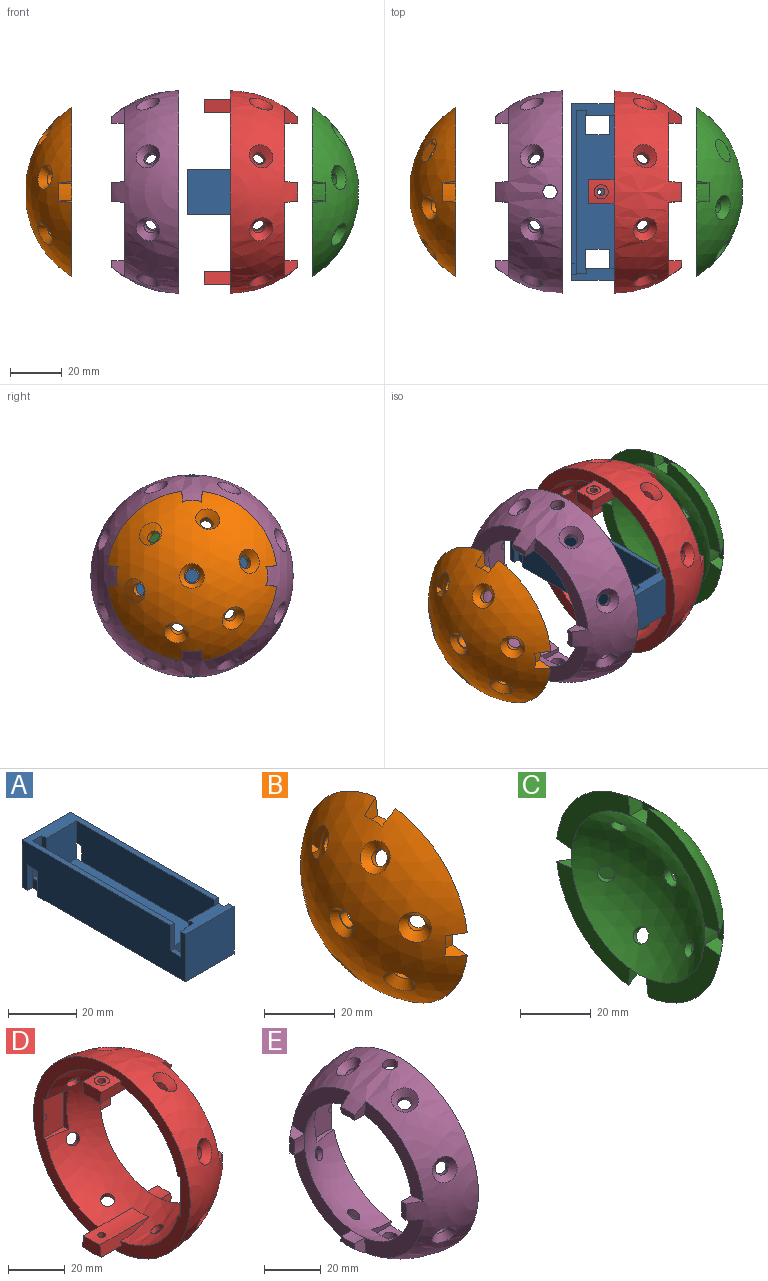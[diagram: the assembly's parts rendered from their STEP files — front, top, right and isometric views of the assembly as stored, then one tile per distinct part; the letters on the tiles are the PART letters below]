
ASSEMBLY  parts=5 mates=4
PART A: 43 faces, bbox 20x67.9x17 mm
  f0: plane 61.42x20mm, normal (0,0,1), area 280.7mm2, adj f1,f4,f6,f7,f10,f11,f14,f15
  f1: plane 67.93x17mm, normal (-1,0,0), area 1075.1mm2, adj f0,f3,f8,f9,f10,f35,f36,f37
  f2: plane 63x16.5mm, normal (0,0,1), area 848.9mm2, adj f5,f6,f7,f11,f12,f13,f14,f15
  f3: plane 67.93x20mm, normal (0,0,-1), area 1193.3mm2, adj f1,f4,f9,f10,f17,f18,f19,f20
  f4: plane 67.93x17mm, normal (1,0,0), area 1075.1mm2, adj f0,f3,f8,f9,f10,f27,f28,f29
  f5: plane 13.5x12.56mm, normal (0,1,0), area 167.2mm2, adj f2,f6,f8,f13,f16,f32,f34
  f6: plane 59x13.5mm, normal (-1,0,0), area 765.7mm2, adj f0,f2,f5,f7,f28,f29,f33,f34
  f7: plane 13.5x12.56mm, normal (0,-1,0), area 168.1mm2, adj f0,f2,f6,f14,f21,f29,f30
  f8: plane 20x4.46mm, normal (0,0,1), area 72.6mm2, adj f1,f4,f5,f9,f12,f13,f31,f32
  f9: plane 20x17mm, normal (0,-1,0), area 340mm2, adj f1,f3,f4,f8
  f10: plane 20x17mm, normal (0,1,0), area 340mm2, adj f0,f1,f3,f4
  f11: plane 63x13.5mm, normal (1,0,0), area 790mm2, adj f0,f2,f12,f15,f36,f37,f40,f41
  f12: plane 13.5x3.94mm, normal (0,1,0), area 50.9mm2, adj f2,f8,f11,f13,f41,f42
  f13: plane 13.5x2mm, normal (-1,0,0), area 27mm2, adj f2,f5,f8,f12,f16
  f14: plane 13.5x2mm, normal (-1,0,0), area 27mm2, adj f0,f2,f7,f15,f21
  f15: plane 13.5x3.94mm, normal (0,-1,0), area 51.8mm2, adj f0,f2,f11,f14,f37,f38
  f16: plane 8.81x0.51mm, normal (0,0,-1), area 4.5mm2, adj f5,f13,f18,f19
  f17: plane 9x3.5mm, normal (0,-1,0), area 31.5mm2, adj f2,f3,f18,f20
  f18: plane 7.87x3.5mm, normal (-1,0,0), area 27.6mm2, adj f2,f3,f16,f17,f19
  f19: plane 9x3.5mm, normal (0,1,0), area 31.5mm2, adj f2,f3,f16,f18,f20
  f20: plane 7.87x3.5mm, normal (1,0,0), area 27.6mm2, adj f2,f3,f17,f19
  f21: plane 8.81x0.51mm, normal (0,0,-1), area 4.5mm2, adj f7,f14,f22,f25
  f22: plane 7.87x3.5mm, normal (-1,0,0), area 27.6mm2, adj f2,f3,f21,f23,f25
  f23: plane 9x3.5mm, normal (0,1,0), area 31.5mm2, adj f2,f3,f22,f24
  f24: plane 7.87x3.5mm, normal (1,0,0), area 27.6mm2, adj f2,f3,f23,f25
  f25: plane 9x3.5mm, normal (0,-1,0), area 31.5mm2, adj f2,f3,f21,f22,f24
  f26: cylinder r=1.4mm len=3.5mm, axis (0,0,1), area 30.7mm2, adj f2,f3
  f27: plane 9.15x2mm, normal (0,-1,0), area 18.3mm2, adj f3,f4,f29,f30
  f28: plane 9.15x2mm, normal (0,1,0), area 16.9mm2, adj f2,f3,f4,f6,f29,f30
  f29: plane 4.35x2mm, normal (0,0,-1), area 8.2mm2, adj f4,f6,f7,f27,f28,f30
  f30: plane 9.15x4.35mm, normal (1,0,0), area 27.6mm2, adj f2,f3,f7,f27,f28,f29
  f31: plane 9.15x2mm, normal (0,1,0), area 18.3mm2, adj f4,f8,f32,f34
  f32: plane 9.15x2.31mm, normal (1,0,0), area 21.2mm2, adj f5,f8,f31,f34
  f33: plane 9.15x1.75mm, normal (0,-1,0), area 16mm2, adj f0,f4,f6,f34
  f34: plane 4.35x2mm, normal (0,0,1), area 8.2mm2, adj f4,f5,f6,f31,f32,f33
  f35: plane 9.15x2mm, normal (0,-1,0), area 18.3mm2, adj f1,f3,f37,f38
  f36: plane 9.15x2mm, normal (0,1,0), area 16.9mm2, adj f1,f2,f3,f11,f37,f38
  f37: plane 4.35x2mm, normal (0,0,-1), area 7.7mm2, adj f1,f11,f15,f35,f36,f38
  f38: plane 9.15x4.35mm, normal (-1,0,0), area 16.3mm2, adj f2,f3,f15,f35,f36,f37
  f39: plane 9.15x2mm, normal (0,1,0), area 18.3mm2, adj f1,f8,f41,f42
  f40: plane 9.15x1.75mm, normal (0,-1,0), area 16mm2, adj f0,f1,f11,f41
  f41: plane 4.35x2mm, normal (0,0,1), area 7.7mm2, adj f1,f11,f12,f39,f40,f42
  f42: plane 9.15x0.31mm, normal (-1,0,0), area 2.9mm2, adj f8,f12,f39,f41
PART B: 38 faces, bbox 28.1x65.9x66.2 mm
  f0: sphere r=39mm, area 3715.4mm2, adj f1,f2,f3,f4,f6,f10,f12,f14
  f1: plane 29.36x29.36mm, normal (1,0,0), area 242.1mm2, adj f0,f5,f24,f28
  f2: plane 29.36x29.36mm, normal (1,0,0), area 242.1mm2, adj f0,f5,f23,f34
  f3: plane 29.36x29.36mm, normal (1,0,0), area 242.1mm2, adj f0,f5,f27,f32
  f4: plane 29.36x29.36mm, normal (1,0,0), area 242.1mm2, adj f0,f5,f31,f35
  f5: sphere r=34mm, area 2634mm2, adj f1,f2,f3,f4,f9,f11,f13,f15
  f6: cone r=2.5mm half-angle=39.8deg, axis (-1,0,0), area 69.3mm2, adj f0,f7
  f7: plane 5.83x5.83mm, normal (-1,0,0), area 7.1mm2, adj f6,f8
  f8: cylinder r=2.5mm len=5mm, axis (-1,0,0), area 40.7mm2, adj f7,f9
  f9: plane 5.21x5.21mm, normal (1,0,0), area 1.7mm2, adj f5,f8
  f10: cone r=2.5mm half-angle=39.8deg, axis (-0.81,-0.41,-0.42), area 80.4mm2, adj f0,f11
  f11: cylinder r=2.5mm len=5.42mm, axis (-0.81,-0.41,-0.42), area 32.9mm2, adj f5,f10
  f12: cone r=2.5mm half-angle=39.8deg, axis (-0.81,0.41,0.42), area 80.4mm2, adj f0,f13
  f13: cylinder r=2.5mm len=5.42mm, axis (-0.81,0.41,0.42), area 32.9mm2, adj f5,f12
  f14: cone r=2.5mm half-angle=39.8deg, axis (-0.81,0.16,-0.57), area 80.4mm2, adj f0,f15
  f15: cylinder r=2.5mm len=5.31mm, axis (-0.81,0.16,-0.57), area 32.9mm2, adj f5,f14
  f16: cone r=2.5mm half-angle=39.8deg, axis (-0.81,-0.16,0.57), area 80.4mm2, adj f0,f17
  f17: cylinder r=2.5mm len=5.31mm, axis (-0.81,-0.16,0.57), area 32.9mm2, adj f5,f16
  f18: cone r=2.5mm half-angle=39.8deg, axis (-0.81,0.57,-0.15), area 80.4mm2, adj f0,f19
  f19: cylinder r=2.5mm len=5.3mm, axis (-0.81,0.57,-0.15), area 32.9mm2, adj f5,f18
  f20: cone r=2.5mm half-angle=39.8deg, axis (-0.81,-0.57,0.15), area 80.4mm2, adj f0,f21
  f21: cylinder r=2.5mm len=5.3mm, axis (-0.81,-0.57,0.15), area 32.9mm2, adj f5,f20
  f22: plane 7.73x3.18mm, normal (1,0,0), area 15.9mm2, adj f0,f23,f24,f25
  f23: plane 6.21x5.13mm, normal (0,-0.12,0.99), area 21.7mm2, adj f0,f2,f22,f25
  f24: plane 6.21x5.13mm, normal (0,-0.12,-0.99), area 21.7mm2, adj f0,f1,f22,f25
  f25: cylinder r=26.74mm len=6.52mm, axis (1,0,0), area 32.7mm2, adj f5,f22,f23,f24
  f26: plane 7.38x2.82mm, normal (1,0,0), area 15.9mm2, adj f0,f27,f28,f29
  f27: plane 6.1x5.02mm, normal (0,-0.99,0.12), area 21.7mm2, adj f0,f3,f26,f29
  f28: plane 6.1x5.02mm, normal (0,0.99,0.12), area 21.7mm2, adj f0,f1,f26,f29
  f29: cylinder r=26.74mm len=6.52mm, axis (1,0,0), area 32.7mm2, adj f5,f26,f27,f28
  f30: plane 7.73x3.18mm, normal (1,0,0), area 15.9mm2, adj f0,f31,f32,f33
  f31: plane 6.21x5.13mm, normal (0,0.12,0.99), area 21.7mm2, adj f0,f4,f30,f33
  f32: plane 6.21x5.13mm, normal (0,0.12,-0.99), area 21.7mm2, adj f0,f3,f30,f33
  f33: cylinder r=26.74mm len=6.52mm, axis (1,0,0), area 32.7mm2, adj f5,f30,f31,f32
  f34: plane 6.1x5.02mm, normal (0,0.99,-0.12), area 21.7mm2, adj f0,f2,f36,f37
  f35: plane 6.1x5.02mm, normal (0,-0.99,-0.12), area 21.7mm2, adj f0,f4,f36,f37
  f36: plane 7.38x2.82mm, normal (1,0,0), area 15.9mm2, adj f0,f34,f35,f37
  f37: cylinder r=26.74mm len=6.52mm, axis (1,0,0), area 32.7mm2, adj f5,f34,f35,f36
PART C: 38 faces, bbox 28.1x65.9x66.2 mm
  f0: plane 29.36x29.36mm, normal (-1,0,0), area 242.1mm2, adj f4,f5,f24,f35
  f1: plane 29.36x29.36mm, normal (-1,0,0), area 242.1mm2, adj f4,f5,f23,f28
  f2: plane 29.36x29.36mm, normal (-1,0,0), area 242.1mm2, adj f4,f5,f27,f32
  f3: plane 29.36x29.36mm, normal (-1,0,0), area 242.1mm2, adj f4,f5,f31,f34
  f4: sphere r=34mm, area 2712.6mm2, adj f0,f1,f2,f3,f9,f11,f13,f15
  f5: sphere r=39mm, area 3715.3mm2, adj f0,f1,f2,f3,f6,f10,f12,f14
  f6: cone r=2.5mm half-angle=39.8deg, axis (1,0,0), area 69.3mm2, adj f5,f7
  f7: plane 5.83x5.83mm, normal (1,0,0), area 7.1mm2, adj f6,f8
  f8: cylinder r=2.5mm len=5mm, axis (1,0,0), area 40.7mm2, adj f7,f9
  f9: plane 5.21x5.21mm, normal (-1,0,0), area 1.7mm2, adj f4,f8
  f10: cone r=2.5mm half-angle=39.8deg, axis (0.81,-0.41,-0.42), area 80.4mm2, adj f5,f11
  f11: cylinder r=2.5mm len=5.42mm, axis (0.81,-0.41,-0.42), area 32.9mm2, adj f4,f10
  f12: cone r=2.5mm half-angle=39.8deg, axis (0.81,0.41,0.42), area 80.4mm2, adj f5,f13
  f13: cylinder r=2.5mm len=5.42mm, axis (0.81,0.41,0.42), area 32.9mm2, adj f4,f12
  f14: cone r=2.5mm half-angle=39.8deg, axis (0.81,0.16,-0.57), area 80.4mm2, adj f5,f15
  f15: cylinder r=2.5mm len=5.31mm, axis (0.81,0.16,-0.57), area 32.9mm2, adj f4,f14
  f16: cone r=2.5mm half-angle=39.8deg, axis (0.81,-0.16,0.57), area 80.4mm2, adj f5,f17
  f17: cylinder r=2.5mm len=5.31mm, axis (0.81,-0.16,0.57), area 32.9mm2, adj f4,f16
  f18: cone r=2.5mm half-angle=39.8deg, axis (0.81,0.57,-0.15), area 80.4mm2, adj f5,f19
  f19: cylinder r=2.5mm len=5.3mm, axis (0.81,0.57,-0.15), area 32.9mm2, adj f4,f18
  f20: cone r=2.5mm half-angle=39.8deg, axis (0.81,-0.57,0.15), area 80.4mm2, adj f5,f21
  f21: cylinder r=2.5mm len=5.3mm, axis (0.81,-0.57,0.15), area 32.9mm2, adj f4,f20
  f22: plane 7.73x3.18mm, normal (-1,0,0), area 15.9mm2, adj f5,f23,f24,f25
  f23: plane 6.21x5.13mm, normal (0,-0.12,-0.99), area 21.7mm2, adj f1,f5,f22,f25
  f24: plane 6.21x5.13mm, normal (0,-0.12,0.99), area 21.7mm2, adj f0,f5,f22,f25
  f25: cylinder r=26.74mm len=6.52mm, axis (-1,0,0), area 32.7mm2, adj f4,f22,f23,f24
  f26: plane 7.38x2.82mm, normal (-1,0,0), area 15.9mm2, adj f5,f27,f28,f29
  f27: plane 6.1x5.02mm, normal (0,-0.99,0.12), area 21.7mm2, adj f2,f5,f26,f29
  f28: plane 6.1x5.02mm, normal (0,0.99,0.12), area 21.7mm2, adj f1,f5,f26,f29
  f29: cylinder r=26.74mm len=6.52mm, axis (-1,0,0), area 32.7mm2, adj f4,f26,f27,f28
  f30: plane 7.73x3.18mm, normal (-1,0,0), area 15.9mm2, adj f5,f31,f32,f33
  f31: plane 6.21x5.13mm, normal (0,0.12,0.99), area 21.7mm2, adj f3,f5,f30,f33
  f32: plane 6.21x5.13mm, normal (0,0.12,-0.99), area 21.7mm2, adj f2,f5,f30,f33
  f33: cylinder r=26.74mm len=6.52mm, axis (-1,0,0), area 32.7mm2, adj f4,f30,f31,f32
  f34: plane 6.1x5.02mm, normal (0,-0.99,-0.12), area 21.7mm2, adj f3,f5,f36,f37
  f35: plane 6.1x5.02mm, normal (0,0.99,-0.12), area 21.7mm2, adj f0,f5,f36,f37
  f36: plane 7.38x2.82mm, normal (-1,0,0), area 15.9mm2, adj f5,f34,f35,f37
  f37: cylinder r=26.74mm len=6.52mm, axis (-1,0,0), area 32.7mm2, adj f4,f34,f35,f36
PART D: 69 faces, bbox 49x78x78 mm
  f0: cylinder r=30.8mm len=24.2mm, axis (-1,0,0), area 188.5mm2, adj f23,f34,f35,f36,f68
  f1: cylinder r=35.8mm len=10mm, axis (-1,0,0), area 70.1mm2, adj f6,f23,f34,f36,f65,f66,f67
  f2: cylinder r=35.8mm len=10mm, axis (-1,0,0), area 70.1mm2, adj f6,f25,f37,f39,f61,f62,f63
  f3: sphere r=34mm, area 4mm2, adj f6,f58
  f4: sphere r=34mm, area 4mm2, adj f6,f53
  f5: sphere r=34mm, area 3727.2mm2, adj f6,f19,f20,f21,f22,f26,f27,f28
  f6: plane 78x78mm, normal (-1,0,0), area 1102.7mm2, adj f1,f2,f3,f4,f5,f34,f36,f37
  f7: plane 6.1x5.02mm, normal (0,0.99,0.12), area 21.7mm2, adj f9,f22,f48,f49
  f8: plane 6.1x5.02mm, normal (0,-0.99,0.12), area 21.7mm2, adj f9,f19,f48,f49
  f9: plane 7.09x2.53mm, normal (1,0,0), area 15.9mm2, adj f7,f8,f48,f49
  f10: plane 6.08x5mm, normal (0,-0.12,-0.99), area 21.7mm2, adj f12,f22,f48,f50
  f11: plane 6.08x5mm, normal (0,-0.12,0.99), area 21.7mm2, adj f12,f21,f48,f50
  f12: plane 7.09x2.53mm, normal (1,0,0), area 15.9mm2, adj f10,f11,f48,f50
  f13: plane 6.1x5.02mm, normal (0,0.99,-0.12), area 21.7mm2, adj f15,f21,f48,f51
  f14: plane 6.1x5.02mm, normal (0,-0.99,-0.12), area 21.7mm2, adj f15,f20,f48,f51
  f15: plane 7.09x2.53mm, normal (1,0,0), area 15.9mm2, adj f13,f14,f48,f51
  f16: plane 6.08x5mm, normal (0,0.12,0.99), area 21.7mm2, adj f18,f20,f48,f52
  f17: plane 6.08x5mm, normal (0,0.12,-0.99), area 21.7mm2, adj f18,f19,f48,f52
  f18: plane 7.09x2.53mm, normal (1,0,0), area 15.9mm2, adj f16,f17,f48,f52
  f19: plane 29.36x29.36mm, normal (1,0,0), area 242.1mm2, adj f5,f8,f17,f48
  f20: plane 29.36x29.36mm, normal (1,0,0), area 242.1mm2, adj f5,f14,f16,f48
  f21: plane 29.36x29.36mm, normal (1,0,0), area 242.1mm2, adj f5,f11,f13,f48
  f22: plane 29.36x29.36mm, normal (1,0,0), area 242.1mm2, adj f5,f7,f10,f48
  f23: plane 9.35x5.26mm, normal (-1,0,0), area 43.6mm2, adj f0,f1,f34,f36
  f24: cylinder r=30.8mm len=24.2mm, axis (-1,0,0), area 188.5mm2, adj f25,f37,f38,f39,f64
  f25: plane 9.35x5.26mm, normal (-1,0,0), area 43.6mm2, adj f2,f24,f37,f39
  f26: cylinder r=2.5mm len=5.42mm, axis (0.31,0.37,-0.88), area 32.9mm2, adj f5,f40
  f27: cylinder r=2.5mm len=5.42mm, axis (0.31,-0.37,0.88), area 32.9mm2, adj f5,f41
  f28: cylinder r=2.5mm len=5.42mm, axis (0.31,-0.36,-0.88), area 32.9mm2, adj f5,f42
  f29: cylinder r=2.5mm len=5.42mm, axis (0.31,0.36,0.88), area 32.9mm2, adj f5,f43
  f30: cylinder r=2.5mm len=5.42mm, axis (0.31,-0.88,-0.37), area 32.9mm2, adj f5,f44
  f31: cylinder r=2.5mm len=5.42mm, axis (0.31,0.88,0.37), area 32.9mm2, adj f5,f45
  f32: cylinder r=2.5mm len=5.42mm, axis (0.31,-0.88,0.36), area 32.9mm2, adj f5,f46
  f33: cylinder r=2.5mm len=5.42mm, axis (0.31,0.88,-0.36), area 32.9mm2, adj f5,f47
  f34: plane 24.2x4.96mm, normal (0,-0.99,0.13), area 81mm2, adj f0,f1,f5,f6,f23,f35
  f35: plane 8.06x0.36mm, normal (1,0,0), area 0.7mm2, adj f0,f5,f34,f36
  f36: plane 24.2x4.96mm, normal (0,0.99,0.13), area 81mm2, adj f0,f1,f5,f6,f23,f35
  f37: plane 24.2x4.96mm, normal (0,0.99,-0.13), area 81mm2, adj f2,f5,f6,f24,f25,f38
  f38: plane 8.06x0.36mm, normal (1,0,0), area 0.7mm2, adj f5,f24,f37,f39
  f39: plane 24.2x4.96mm, normal (0,-0.99,-0.13), area 81mm2, adj f2,f5,f6,f24,f25,f38
  f40: cone r=2.5mm half-angle=39.8deg, axis (0.31,0.37,-0.88), area 80.4mm2, adj f26,f48
  f41: cone r=2.5mm half-angle=39.8deg, axis (0.31,-0.37,0.88), area 80.4mm2, adj f27,f48
  f42: cone r=2.5mm half-angle=39.8deg, axis (0.31,-0.36,-0.88), area 80.4mm2, adj f28,f48
  f43: cone r=2.5mm half-angle=39.8deg, axis (0.31,0.36,0.88), area 80.4mm2, adj f29,f48
  f44: cone r=2.5mm half-angle=39.8deg, axis (0.31,-0.88,-0.37), area 80.4mm2, adj f30,f48
  f45: cone r=2.5mm half-angle=39.8deg, axis (0.31,0.88,0.37), area 80.4mm2, adj f31,f48
  f46: cone r=2.5mm half-angle=39.8deg, axis (0.31,-0.88,0.36), area 80.4mm2, adj f32,f48
  f47: cone r=2.5mm half-angle=39.8deg, axis (0.31,0.88,-0.36), area 80.4mm2, adj f33,f48
  f48: sphere r=39mm, area 4765.4mm2, adj f6,f7,f8,f9,f10,f11,f12,f13
  f49: cylinder r=26.74mm len=6.52mm, axis (-1,0,0), area 32.7mm2, adj f5,f7,f8,f9
  f50: cylinder r=26.74mm len=6.52mm, axis (-1,0,0), area 32.7mm2, adj f5,f10,f11,f12
  f51: cylinder r=26.74mm len=6.52mm, axis (-1,0,0), area 32.7mm2, adj f5,f13,f14,f15
  f52: cylinder r=26.74mm len=6.52mm, axis (-1,0,0), area 32.7mm2, adj f5,f16,f17,f18
  f53: plane 17x10mm, normal (0,-1,0), area 166mm2, adj f4,f6,f54,f55,f56
  f54: plane 10x2.6mm, normal (0,0,-1), area 15.6mm2, adj f5,f6,f53,f56
  f55: plane 10x2.6mm, normal (0,0,1), area 15.6mm2, adj f5,f6,f53,f56
  f56: plane 17x2.6mm, normal (-1,0,0), area 31.3mm2, adj f5,f53,f54,f55
  f57: plane 10x2.6mm, normal (0,0,-1), area 15.6mm2, adj f5,f6,f58,f60
  f58: plane 17x10mm, normal (0,1,0), area 166mm2, adj f3,f6,f57,f59,f60
  f59: plane 10x2.6mm, normal (0,0,1), area 15.6mm2, adj f5,f6,f58,f60
  f60: plane 17x2.6mm, normal (-1,0,0), area 31.3mm2, adj f5,f57,f58,f59
  f61: cylinder r=2.75mm len=5.35mm, axis (0,0,1), area 0.4mm2, adj f2,f63
  f62: cylinder r=2.75mm len=5.35mm, axis (0,0,1), area 0.4mm2, adj f2,f63
  f63: plane 5.5x5.35mm, normal (0,0,1), area 17mm2, adj f2,f61,f62,f64
  f64: cylinder r=1.45mm len=4.93mm, axis (0,0,1), area 44.8mm2, adj f24,f63
  f65: cylinder r=2.75mm len=5.35mm, axis (0,0,-1), area 0.4mm2, adj f1,f67
  f66: cylinder r=2.75mm len=5.35mm, axis (0,0,-1), area 0.4mm2, adj f1,f67
  f67: plane 5.5x5.35mm, normal (0,0,-1), area 17mm2, adj f1,f65,f66,f68
  f68: cylinder r=1.45mm len=4.93mm, axis (0,0,-1), area 44.8mm2, adj f0,f67
PART E: 63 faces, bbox 39x78x78 mm
  f0: sphere r=39mm, area 4717.5mm2, adj f6,f7,f8,f9,f10,f11,f12,f13
  f1: cylinder r=35.8mm len=10mm, axis (-1,0,0), area 70.1mm2, adj f6,f46,f47,f48,f60,f61,f62
  f2: cylinder r=35.8mm len=10mm, axis (-1,0,0), area 70.1mm2, adj f6,f43,f44,f45,f57,f58,f59
  f3: sphere r=34mm, area 4mm2, adj f6,f54
  f4: sphere r=34mm, area 4mm2, adj f6,f49
  f5: sphere r=34mm, area 3802mm2, adj f6,f19,f20,f21,f22,f23,f24,f25
  f6: plane 78x78mm, normal (1,0,0), area 1102.7mm2, adj f0,f1,f2,f3,f4,f5,f43,f44
  f7: plane 6.1x5.02mm, normal (0,-0.99,0.12), area 21.7mm2, adj f0,f9,f20,f39
  f8: plane 6.1x5.02mm, normal (0,0.99,0.12), area 21.7mm2, adj f0,f9,f22,f39
  f9: plane 7.09x2.53mm, normal (-1,0,0), area 15.9mm2, adj f0,f7,f8,f39
  f10: plane 6.08x5mm, normal (0,-0.12,0.99), area 21.7mm2, adj f0,f12,f21,f40
  f11: plane 6.08x5mm, normal (0,-0.12,-0.99), area 21.7mm2, adj f0,f12,f22,f40
  f12: plane 7.09x2.53mm, normal (-1,0,0), area 15.9mm2, adj f0,f10,f11,f40
  f13: plane 6.1x5.02mm, normal (0,-0.99,-0.12), area 21.7mm2, adj f0,f15,f19,f41
  f14: plane 6.1x5.02mm, normal (0,0.99,-0.12), area 21.7mm2, adj f0,f15,f21,f41
  f15: plane 7.09x2.53mm, normal (-1,0,0), area 15.9mm2, adj f0,f13,f14,f41
  f16: plane 6.08x5mm, normal (0,0.12,-0.99), area 21.7mm2, adj f0,f18,f20,f42
  f17: plane 6.08x5mm, normal (0,0.12,0.99), area 21.7mm2, adj f0,f18,f19,f42
  f18: plane 7.09x2.53mm, normal (-1,0,0), area 15.9mm2, adj f0,f16,f17,f42
  f19: plane 29.36x29.36mm, normal (-1,0,0), area 242.1mm2, adj f0,f5,f13,f17
  f20: plane 29.36x29.36mm, normal (-1,0,0), area 242.1mm2, adj f0,f5,f7,f16
  f21: plane 29.36x29.36mm, normal (-1,0,0), area 242.1mm2, adj f0,f5,f10,f14
  f22: plane 29.36x29.36mm, normal (-1,0,0), area 242.1mm2, adj f0,f5,f8,f11
  f23: cylinder r=2.5mm len=5.42mm, axis (-0.31,-0.37,0.88), area 32.9mm2, adj f5,f32
  f24: cylinder r=2.5mm len=5.42mm, axis (-0.31,0.36,0.88), area 32.9mm2, adj f5,f34
  f25: cylinder r=2.5mm len=5.42mm, axis (-0.31,0.88,0.37), area 32.9mm2, adj f5,f36
  f26: cylinder r=2.5mm len=5.42mm, axis (-0.31,0.88,-0.36), area 32.9mm2, adj f5,f38
  f27: cylinder r=2.5mm len=5.42mm, axis (-0.31,-0.88,0.36), area 32.9mm2, adj f5,f37
  f28: cylinder r=2.5mm len=5.42mm, axis (-0.31,-0.88,-0.37), area 32.9mm2, adj f5,f35
  f29: cylinder r=2.5mm len=5.42mm, axis (-0.31,-0.36,-0.88), area 32.9mm2, adj f5,f33
  f30: cylinder r=2.5mm len=5.42mm, axis (-0.31,0.37,-0.88), area 32.9mm2, adj f5,f31
  f31: cone r=2.5mm half-angle=39.8deg, axis (-0.31,0.37,-0.88), area 80.4mm2, adj f0,f30
  f32: cone r=2.5mm half-angle=39.8deg, axis (-0.31,-0.37,0.88), area 80.4mm2, adj f0,f23
  f33: cone r=2.5mm half-angle=39.8deg, axis (-0.31,-0.36,-0.88), area 80.4mm2, adj f0,f29
  f34: cone r=2.5mm half-angle=39.8deg, axis (-0.31,0.36,0.88), area 80.4mm2, adj f0,f24
  f35: cone r=2.5mm half-angle=39.8deg, axis (-0.31,-0.88,-0.37), area 80.4mm2, adj f0,f28
  f36: cone r=2.5mm half-angle=39.8deg, axis (-0.31,0.88,0.37), area 80.4mm2, adj f0,f25
  f37: cone r=2.5mm half-angle=39.8deg, axis (-0.31,-0.88,0.36), area 80.4mm2, adj f0,f27
  f38: cone r=2.5mm half-angle=39.8deg, axis (-0.31,0.88,-0.36), area 80.4mm2, adj f0,f26
  f39: cylinder r=26.74mm len=6.52mm, axis (1,0,0), area 32.7mm2, adj f5,f7,f8,f9
  f40: cylinder r=26.74mm len=6.52mm, axis (1,0,0), area 32.7mm2, adj f5,f10,f11,f12
  f41: cylinder r=26.74mm len=6.52mm, axis (1,0,0), area 32.7mm2, adj f5,f13,f14,f15
  f42: cylinder r=26.74mm len=6.52mm, axis (1,0,0), area 32.7mm2, adj f5,f16,f17,f18
  f43: plane 10x3.28mm, normal (0,-0.99,0.13), area 23mm2, adj f2,f5,f6,f45
  f44: plane 10x3.28mm, normal (0,0.99,0.13), area 23mm2, adj f2,f5,f6,f45
  f45: plane 9.35x3.58mm, normal (1,0,0), area 29.5mm2, adj f2,f5,f43,f44
  f46: plane 9.35x3.58mm, normal (1,0,0), area 29.5mm2, adj f1,f5,f47,f48
  f47: plane 10x3.28mm, normal (0,0.99,-0.13), area 23mm2, adj f1,f5,f6,f46
  f48: plane 10x3.28mm, normal (0,-0.99,-0.13), area 23mm2, adj f1,f5,f6,f46
  f49: plane 17x10mm, normal (0,-1,0), area 166mm2, adj f4,f6,f50,f51,f52
  f50: plane 10x2.6mm, normal (0,0,-1), area 15.6mm2, adj f5,f6,f49,f52
  f51: plane 10x2.6mm, normal (0,0,1), area 15.6mm2, adj f5,f6,f49,f52
  f52: plane 17x2.6mm, normal (1,0,0), area 31.3mm2, adj f5,f49,f50,f51
  f53: plane 10x2.6mm, normal (0,0,1), area 15.6mm2, adj f5,f6,f54,f56
  f54: plane 17x10mm, normal (0,1,0), area 166mm2, adj f3,f6,f53,f55,f56
  f55: plane 10x2.6mm, normal (0,0,-1), area 15.6mm2, adj f5,f6,f54,f56
  f56: plane 17x2.6mm, normal (1,0,0), area 31.3mm2, adj f5,f53,f54,f55
  f57: cylinder r=2.75mm len=5.5mm, axis (0,0,1), area 49mm2, adj f0,f2,f58,f59
  f58: plane 1.28x0.08mm, normal (0,0,1), area 0.1mm2, adj f2,f57
  f59: plane 1.28x0.08mm, normal (0,0,1), area 0.1mm2, adj f2,f57
  f60: cylinder r=2.75mm len=5.5mm, axis (0,0,-1), area 48.9mm2, adj f0,f1,f61,f62
  f61: plane 1.28x0.08mm, normal (0,0,-1), area 0.1mm2, adj f1,f60
  f62: plane 1.28x0.08mm, normal (0,0,-1), area 0.1mm2, adj f1,f60
PLACE A t=(-6.36,0.57,0.39)mm
PLACE B t=(-39.96,0.57,0.39)mm
PLACE C t=(10.65,0.57,0.39)mm
PLACE D t=(0.04,0.57,0.39)mm fixed
PLACE E t=(-19.67,0.57,0.39)mm
MATE slider D.f49 <-> A.f4  axis (-1,0,0) through (10.04,0.57,0.39)mm
MATE slider D.f49 <-> E.f39  axis (-1,0,0) through (0.04,0.57,0.39)mm
MATE slider B.f37 <-> E.f39  axis (1,0,0) through (-60.96,0.57,0.39)mm
MATE slider C.f37 <-> D.f49  axis (-1,0,0) through (31.65,0.57,0.39)mm
